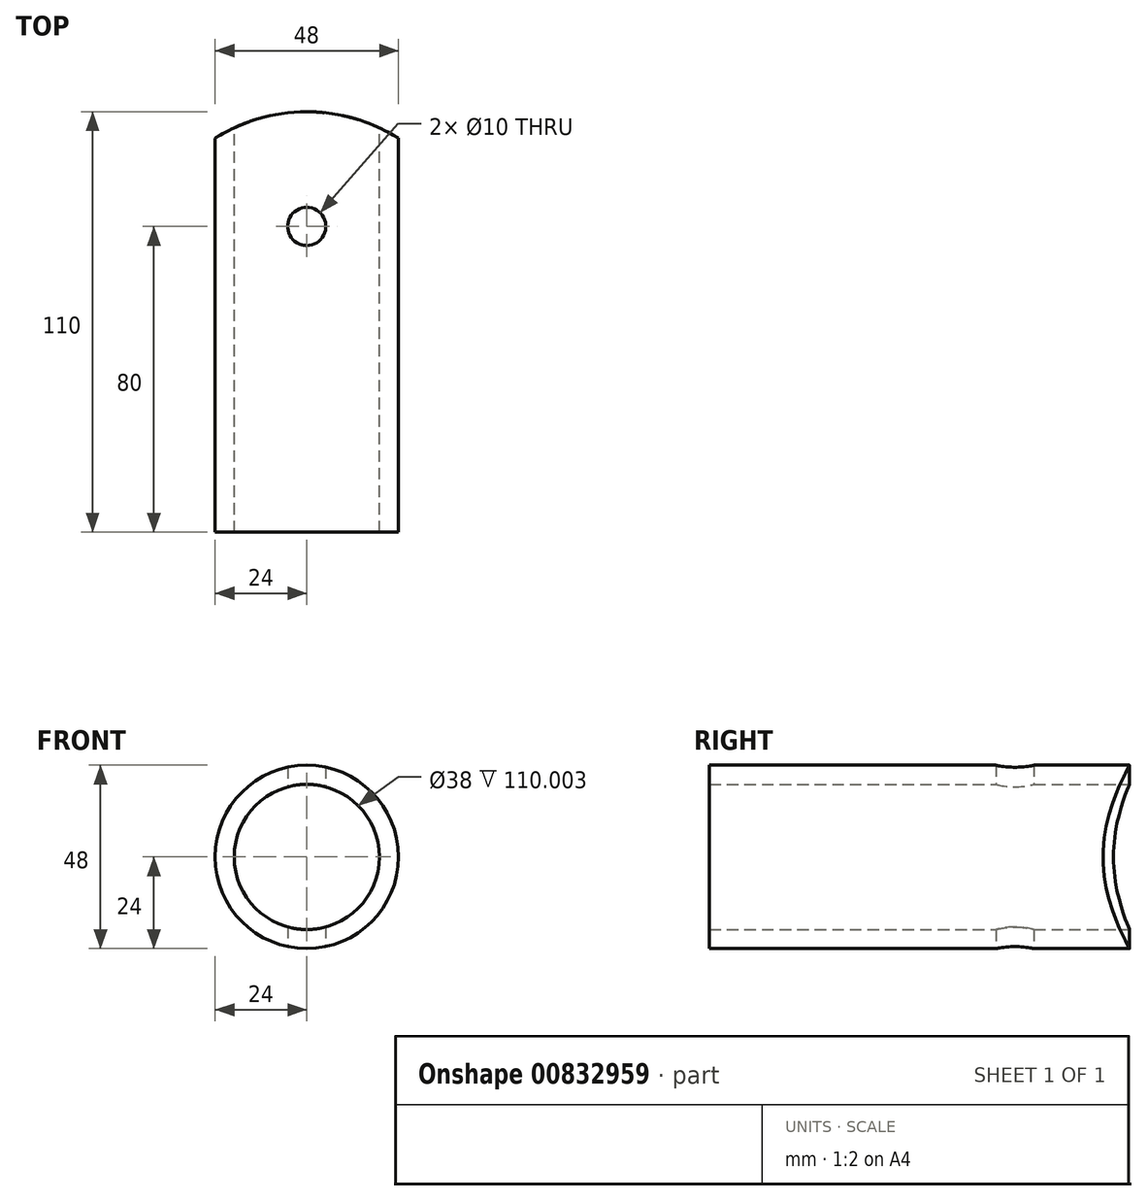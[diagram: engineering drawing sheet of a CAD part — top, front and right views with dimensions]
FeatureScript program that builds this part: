
annotation { "Feature Type Name" : "Feature", "Feature Type Description" : "" }
export const myFeature = defineFeature(function(context is Context, id is Id, definition is map)
    precondition{}
    {
        {
            var Q0;
            Q0=qCreatedBy(makeId("Front.planeOp"),FACE);
            var sketch = newSketch(context, id + "F0", { "sketchPlane" : qUnion([Q0])});
            skCircle(sketch, "E0", {"center": v(0, 0) * mm, "radius": 24 * mm});
            skCircle(sketch, "E1", {"center": v(0, 0) * mm, "radius": 19 * mm});
            skSolve(sketch);
        }
        {
            var Q0;
            Q0=makeQuery(id+"F0.imprint","IMPRINT",FACE,{"disambiguationData":[TD([[makeQuery(id+"F0.imprint","IMPRINT",EDGE,{"derivedFrom":sQuery(id+"F0.wireOp",EDGE,"E0")}),1.0]])]});
            extrude(context, id + "F1", {"entities" : qUnion([Q0]), "depth" : 110 * mm, "offsetDistance" : 25 * mm});
        }
        {
            var Q0;
            Q0=qCreatedBy(makeId("Top.planeOp"),FACE);
            var sketch = newSketch(context, id + "F2", { "sketchPlane" : qUnion([Q0])});
            skCircle(sketch, "E2", {"center": v(0, -25) * mm, "radius": 5 * mm});
            skLineSegment(sketch, "E3", {"start": v(0, 0) * mm, "end": v(0, -57.6) * mm, "construction": true});
            skLineSegment(sketch, "E4", {"start": v(0, -25) * mm, "end": v(-40.42, -25) * mm, "construction": true});
            skLineSegment(sketch, "E5", {"start": v(-40.42, -25) * mm, "end": v(30.62, -25) * mm, "construction": true});
            skSolve(sketch);
        }
        {
            var Q0;
            Q0=qCreatedBy(makeId("Top.planeOp"),FACE);
            var Q1;
            Q1 = qBodyType(qCreatedBy(id + "F4" ,EDGE), BodyType.WIRE);
            cPlane(context, id + "F3", {"entities" : qUnion([Q0, Q1]), "cplaneType" : CPlaneType.OFFSET, "offset" : 20 * mm, "oppositeDirection" : true, "width" : 150 * mm, "height" : 150 * mm});
        }
        {
            var Q0;
            Q0=qCreatedBy(id+"F3.planeOp",FACE);
            var sketch = newSketch(context, id + "F4", { "sketchPlane" : qUnion([Q0])});
            skCircle(sketch, "E6", {"center": v(0, -30) * mm, "radius": 5 * mm});
            skLineSegment(sketch, "E7", {"start": v(0, 0) * mm, "end": v(0, -45) * mm, "construction": true});
            skArc(sketch, "E8", {"start": v(21.4, -5.41) * mm, "mid": v(11.04, -1.37) * mm, "end": v(0, 0) * mm});
            skPoint(sketch, "E9.center.orphan", {"position": v(0, -90.88) * mm});
            skArc(sketch, "E10", {"start": v(24.74, -7.41) * mm, "mid": v(-0.4, 0) * mm, "end": v(-25.42, -7.87) * mm});
            skLineSegment(sketch, "E11.top", {"start": v(-25.42, 8.4) * mm, "end": v(24.74, 8.4) * mm});
            skLineSegment(sketch, "E11.left", {"start": v(-25.42, -7.87) * mm, "end": v(-25.42, 8.4) * mm});
            skLineSegment(sketch, "E11.right", {"start": v(24.74, -7.41) * mm, "end": v(24.74, 8.4) * mm});
            skSolve(sketch);
        }
        {
            var Q0;
            Q0=makeQuery(id+"F4.imprint","IMPRINT",FACE,{"disambiguationData":[TD([[makeQuery(id+"F4.imprint","IMPRINT",EDGE,{"derivedFrom":sQuery(id+"F4.wireOp",EDGE,"E6")}),1.0]])]});
            extrude(context, id + "F5", {"entities" : qUnion([Q0]), "operationType" : NewBodyOperationType.REMOVE, "depth" : 96.8 * mm, "offsetDistance" : 25 * mm, "symmetric" : true});
        }
        {
            var Q0;
            Q0=makeQuery(id+"F4.imprint","IMPRINT",FACE,{"disambiguationData":[TD([[makeQuery(id+"F4.imprint","IMPRINT",EDGE,{"derivedFrom":sQuery(id+"F4.wireOp",EDGE,"E11.top")}),-1.0]])]});
            extrude(context, id + "F6", {"entities" : qUnion([Q0]), "operationType" : NewBodyOperationType.REMOVE, "depth" : 95.6 * mm, "offsetDistance" : 25 * mm, "symmetric" : true});
        }
    });
